# Revit family: Electronics_Desono_Biamp_Surface-Mount-Loudspeaker_MASK2
name_source: partatom
category: Communication Devices
units: mm (PartAtom-declared; Revit-internal decimal feet)

## family parameters
Cut with Voids When Loaded = No
Host = Face
Maintain Annotation Orientation = No
OmniClass Number = 23.85.10.11.14.14.14
OmniClass Title = Loudspeakers
Part Type = Normal
Room Calculation Point = No
Round Connector Dimension = Use Diameter
Shared = No

## types (2) — shared parameters
Connector Description = 2-way Euroblock; 17V 35W 8Ω (140W peak)
Continuous Power Handling Nominal Impedance = 17V; 35W @ 8Ω (140W peak)
Default Elevation = 4' - 0"
Depth = 0' - 4 1/2"
Description = Desono™ MASK2 2.5-Inch Surface Mount Loudspeaker
Environmental = IP60 per IEC 60529
Height = 0' - 3 1/2"
Input Connection = 2-way Euroblock connector
Manufacturer = Biamp
Mounting Provisions = Turn/tilt bracket
Nominal Beamwidth  (H x V) = 110 x 110
Nominal Maximum SPL @ 1m = Peak - 105dB; Continuous - 99dB
Nominal Sensitivity @ 1m = 1W - 84dB; 2.83V - 84dB
Operating Environment = Indoor
Operating Mode = Passive
Operating Range (-10dB) = 125 Hz to 22 kHz
Product Documentation Link = https://downloads.biamp.com
Product Page URL = https://www.biamp.com
Product data url = https://www.bimobject.com
Recommended Accessories = 150 Hz, 12dB/Oct High Pass
Recommended Amplifers = 35W - 70W @ 8Ω (17V - 24V)
Transducers = 1 x 2.5 (64 mm) paper cone
URL = https://www.biamp.com
Weight = 1.10 lb
Width = 0' - 3"

## per-type parameters (varying)
| type | Bracket Material | Grill Material | Housing Material |
| MASK2 B | Biamp - Plastic - Black | Biamp - Plastic - Black(Grid) | Biamp - Plastic - Black |
| MASK2 W | Biamp - Plastic - White | Biamp - Plastic - White(Grid) | Biamp - Plastic - White |

note: column(s) folded — value = type name in every type: Model

## geometry (parser evidence)
native form markers: Sweep x4
no freeform markers — native parametric forms only
